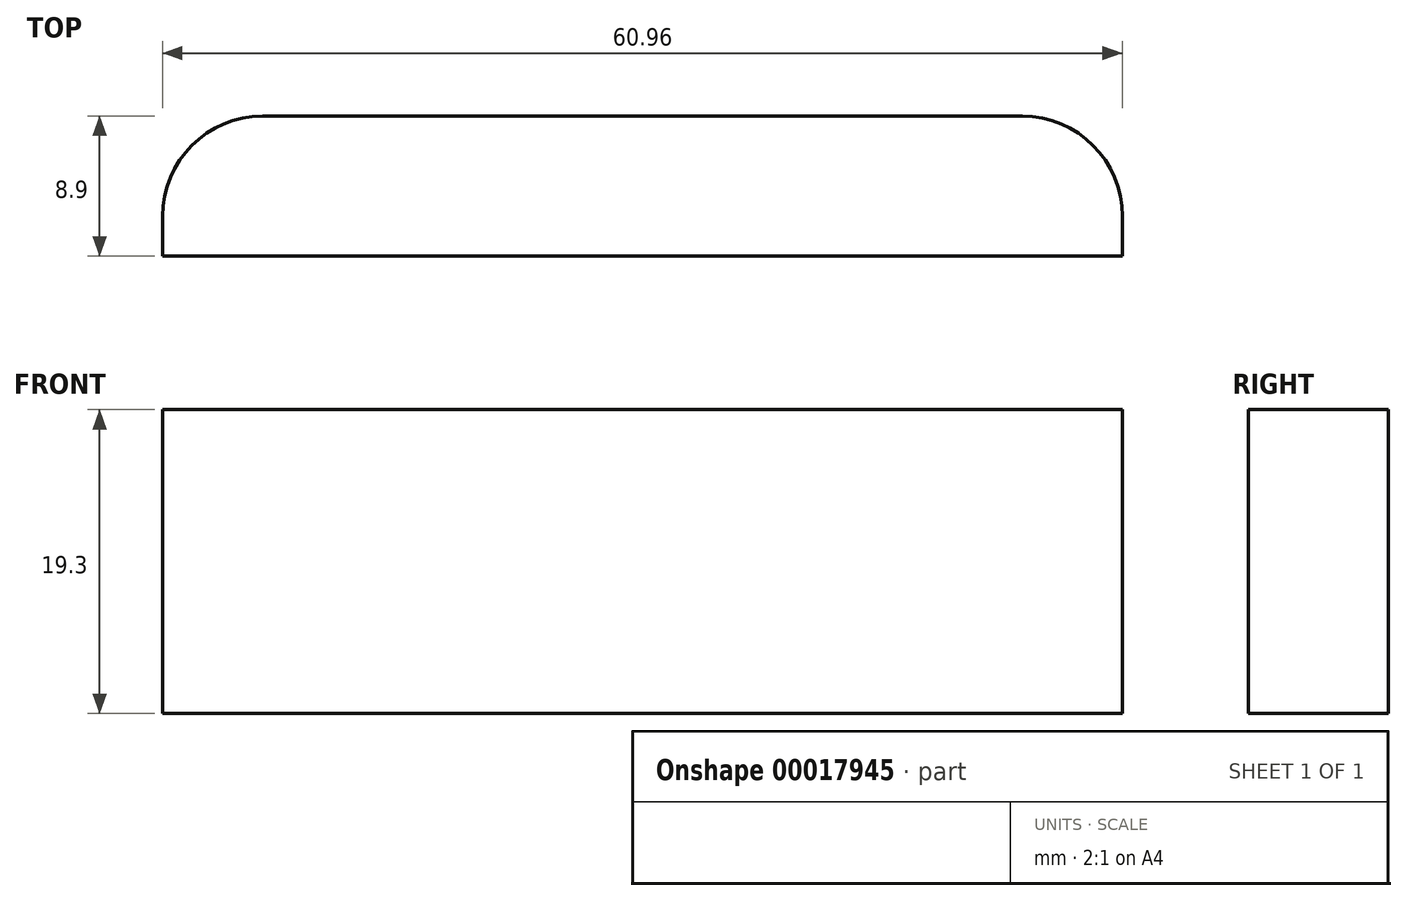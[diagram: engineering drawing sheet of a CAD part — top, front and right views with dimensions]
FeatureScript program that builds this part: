
annotation { "Feature Type Name" : "Feature", "Feature Type Description" : "" }
export const myFeature = defineFeature(function(context is Context, id is Id, definition is map)
    precondition{}
    {
        {
            var Q0;
            Q0=qCreatedBy(makeId("Top.planeOp"),FACE);
            var sketch = newSketch(context, id + "F0", { "sketchPlane" : qUnion([Q0])});
            skLineSegment(sketch, "E0.bottom", {"start": v(30.48, -4.44) * mm, "end": v(-30.48, -4.45) * mm});
            skLineSegment(sketch, "E0.top", {"start": v(30.48, 4.45) * mm, "end": v(-30.48, 4.44) * mm});
            skLineSegment(sketch, "E0.left", {"start": v(30.48, -4.44) * mm, "end": v(30.48, 4.45) * mm});
            skLineSegment(sketch, "E0.right", {"start": v(-30.48, -4.44) * mm, "end": v(-30.48, 4.45) * mm});
            skPoint(sketch, "E0.middle", {"position": v(0, 0) * mm});
            skSolve(sketch);
        }
        {
            var Q0;
            Q0 = qSketchRegion(id + "F0", true);
            extrude(context, id + "F1", {"entities" : qUnion([Q0]), "depth" : 19.3 * mm, "offsetDistance" : 25.4 * mm});
        }
        {
            var Q0;
            Q0=makeQuery(id+"F1.opExtrude","SWEPT_EDGE",EDGE,{"disambiguationData":[OSD([sQuery(id+"F0.wireOp",EDGE,"E0.top"),sQuery(id+"F0.wireOp",EDGE,"E0.right")])]});
            var Q1;
            Q1=makeQuery(id+"F1.opExtrude","SWEPT_EDGE",EDGE,{"disambiguationData":[OSD([sQuery(id+"F0.wireOp",EDGE,"E0.top"),sQuery(id+"F0.wireOp",EDGE,"E0.left")])]});
            fillet(context, id + "F2", {"entities" : qUnion([Q0, Q1]), "radius" : 6.35 * mm, "tangentPropagation" : true, "allowEdgeOverflow" : false});
        }
    });
